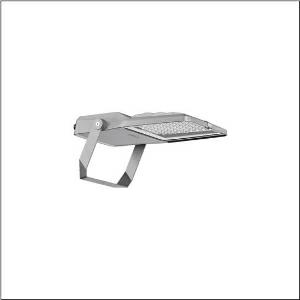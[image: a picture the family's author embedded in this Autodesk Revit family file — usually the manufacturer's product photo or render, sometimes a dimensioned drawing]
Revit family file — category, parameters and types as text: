
# Revit family: floodlight_fl_21_mini___pl64_5xa7775c2e1a_4676
name_source: partatom
category: Lighting Fixtures
units: mm (PartAtom-declared; Revit-internal decimal feet)

## family parameters
Cut with Voids When Loaded = No
Host = Face
Light Source = No
Part Type = Normal
Room Calculation Point = No
Round Connector Dimension = Use Diameter
Shared = No

## types (1)
- --- (1 x LED, 11770 lm, 89 W, 3000K)
    Apparent Load = 89 VA
    CIE Flux Codes = 28 80 98 100 100
    Color Rendering = 70
    Color Temperature = 3000K
    Default Elevation = 1800 mm
    Description = Floodlight FL 21 mini, floodlight, primary light control with lens, of PMMA, primary optical cover: protective disc, of toughened safety glass, transparent, light distribution: PL64, light emission: direct distribution, installation type: surface-mounted, LED, High Power LED, rated luminous flux: 11.770lm, luminous efficacy: 132lm/W, light colour: 730, colour temperature: 3000K, control gear: Smart Interface (Zhaga), control: flexible luminous flux parameterisation, time-dependent luminous flux control, constant luminous flux control, overheat protection, pre-setting: logarithmic dimming characteristic, with terminal, 6-pole, mains connection: 220..240V, AC, 50/60Hz, start of lifetime: 89W, end of service life: 94W, reduction: 43W, luminaire housing, of diecast aluminium, powder-coated, SITECO metallic grey (DB 702S), corrosivity category C5 mid according to DIN EN ISO 12944, suitable for swimming pools, chlorine-resistant, sealing non-destructively replaceable, mounting bracket, of steel, galvanised, powder-coated, SITECO metallic grey (DB 702S), Smart Interface above, protection rating (complete): IP66, insulation class (complete): insulation class II (safety insulation), certification: CE, ENEC, VDE, protection symbol: D, impact resistance: IK08, permissible operating ambient temperature: -40..+40°C, permissible operating ambient temperature for outdoor applications: -40..+50°C, standard: DIN EN 12944, LABS conformity tested according to VDMA 24364:2018-05, packaging unit: 1 piece

Light Distribution: PL64
    Height = 70 mm
    Lamp = 1 x LED
    Lamp Light Flux = 11770 lm
    Lamp Power = 89 W
    Lamp count = 1
    Length = 485 mm
    Luminous efficacy = 132 lm/W
    Manufacturer = Siteco
    ModVariant = No
    Model = 5XA7775C2E1A
    Number of Poles = 1
    OnlyDefault = Yes
    Power Factor = 1
    Product Name = Floodlight FL 21 mini | PL64
    Product group = floodlight | pylon annexe
    ProductGroupID = 6201
    Protection Class = Protection class II
    Protection Degree = IP 66
    RLX_Detail_Level = 1
    RLX_Emergency_Light_Flux = 0 lm
    RLX_Emergency_Type = 0
    RLX_Emergency_Type_DB = No
    RlxData = <blob elided: 96069 chars, md5=ef0d1ee2>
    Socket = socket
    Standby Power = 0 W
    System Light Flux = 11770 lm
    System Power = 89 W
    Type Comments = factory setting: luminous flux: 100 % | dim-lin: 254 | 456 mA
    Type Image = l_1006845.jpg
    URL = http://relux.com
    VarID = @adj_164919
    Voltage = 0 V
    Weight = 0.00 kg
    Width = 337 mm

## geometry (parser evidence)
native form markers: Blend x4, Sweep x11
no freeform markers — native parametric forms only
